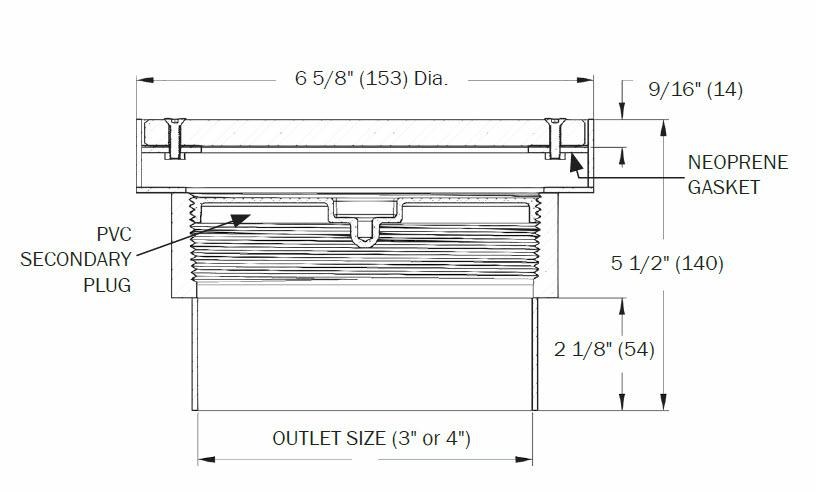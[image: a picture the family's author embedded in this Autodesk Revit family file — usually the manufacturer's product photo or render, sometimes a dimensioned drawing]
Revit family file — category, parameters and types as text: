
# Revit family: P7060-S
name_source: partatom
category: Plumbing Fixtures
revit_build: Autodesk Revit 2018 (Build: 20170223_1515(x64)
units: mm (PartAtom-declared; Revit-internal decimal feet)

## family parameters
Cut with Voids When Loaded = No
Host = Face
Part Type = Normal
Room Calculation Point = No
Round Connector Dimension = Use Radius
Shared = No

## types (2) — shared parameters
Default Elevation = 0' - 0"
Description = 6" SQUARE, TYPE 316 STAINLESS STEEL FABRICATED INDUSTRIAL FLOOR CLEANOUT
Floor Drain Material = Paint - Sherwin Williams Paint - #952C2A - Bellwood Red
MH-501 = No
MH-600 = No
Manufacturer = MIFAB
Model = P7063-S
URL = WWW.MIFAB.COM
zero-valued in all types: CWFU, WFU

## per-type parameters (varying)
| type | MH-301 | MH-401 | Pipe Diameter | Pipe Radius |
| P7063-S_Ø3" | Yes | No | 0' - 3" | 0' - 1 1/2" |
| P7063-S_Ø4" | No | Yes | 0' - 4" | 0' - 2" |

## geometry (parser evidence)
native form markers: Sweep x14
no freeform markers — native parametric forms only
